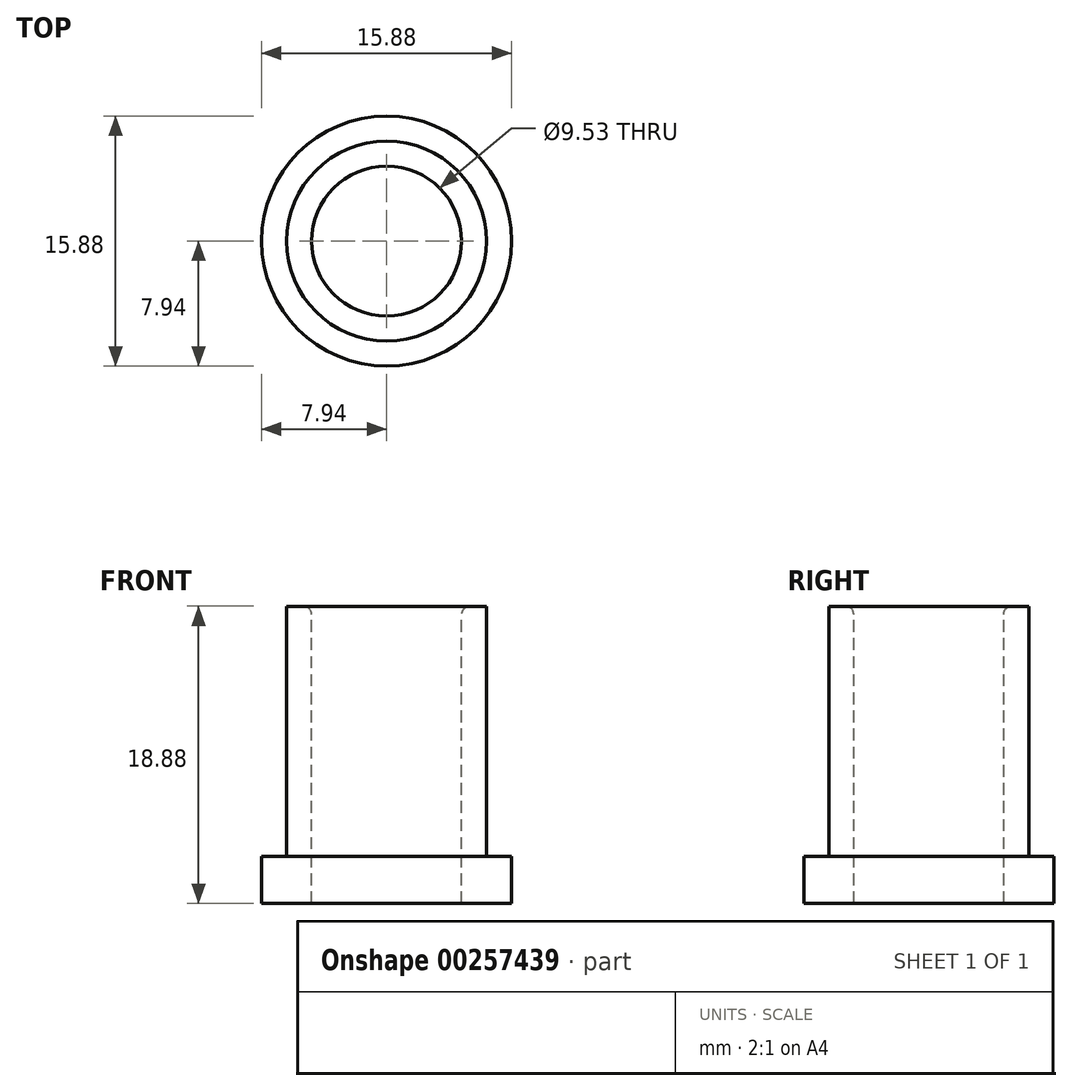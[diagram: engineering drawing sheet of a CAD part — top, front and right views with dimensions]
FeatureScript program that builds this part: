
annotation { "Feature Type Name" : "Feature", "Feature Type Description" : "" }
export const myFeature = defineFeature(function(context is Context, id is Id, definition is map)
    precondition{}
    {
        {
            var Q0;
            Q0=qCreatedBy(makeId("Top.planeOp"),FACE);
            var sketch = newSketch(context, id + "F0", { "sketchPlane" : qUnion([Q0])});
            skCircle(sketch, "E0", {"center": v(0, 0) * mm, "radius": 6.35 * mm});
            skCircle(sketch, "E1", {"center": v(0, 0) * mm, "radius": 7.94 * mm});
            skCircle(sketch, "E2", {"center": v(0, 0) * mm, "radius": 4.76 * mm});
            skSolve(sketch);
        }
        {
            var Q0;
            Q0 = qSketchRegion(id + "F0", true);
            var Q1;
            Q1=makeQuery(id+"F0.imprint","IMPRINT",FACE,{"disambiguationData":[TD([[makeQuery(id+"F0.imprint","IMPRINT",EDGE,{"derivedFrom":sQuery(id+"F0.wireOp",EDGE,"E0")}),1.0]])]});
            extrude(context, id + "F1", {"entities" : qUnion([Q0, Q1]), "oppositeDirection" : true, "depth" : 3 * mm});
        }
        {
            var Q0;
            Q0=makeQuery(id+"F0.imprint","IMPRINT",FACE,{"disambiguationData":[TD([[makeQuery(id+"F0.imprint","IMPRINT",EDGE,{"derivedFrom":sQuery(id+"F0.wireOp",EDGE,"E0")}),1.0]])]});
            extrude(context, id + "F2", {"entities" : qUnion([Q0]), "operationType" : NewBodyOperationType.ADD, "depth" : 15.88 * mm});
        }
        {
            var Q0;
            Q0=makeQuery(id+"F2.opExtrude","CAP_EDGE",EDGE,{"disambiguationData":[OSD([sQuery(id+"F0.wireOp",EDGE,"E2")])],"isStart":false});
            fillet(context, id + "F3", {"entities" : qUnion([Q0]), "radius" : 0.5 * mm, "tangentPropagation" : true, "allowEdgeOverflow" : false});
        }
    });
